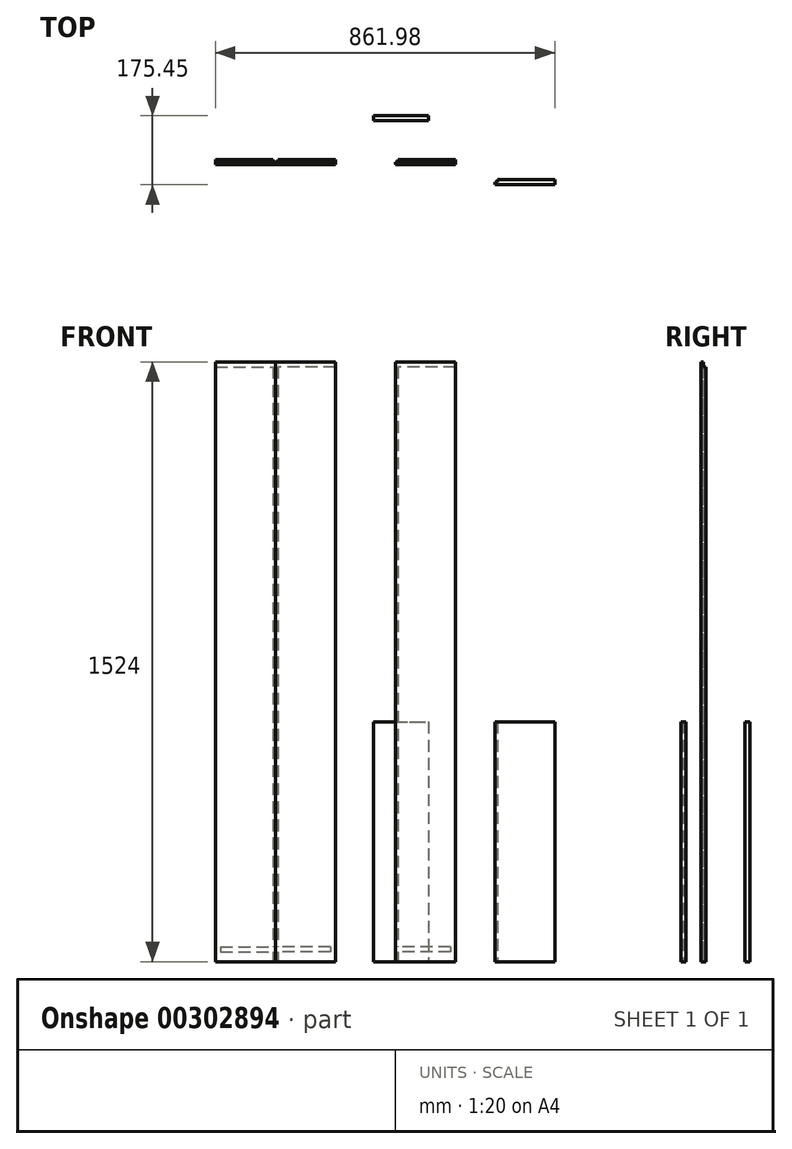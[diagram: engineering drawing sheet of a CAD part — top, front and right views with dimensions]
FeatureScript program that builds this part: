
annotation { "Feature Type Name" : "Feature", "Feature Type Description" : "" }
export const myFeature = defineFeature(function(context is Context, id is Id, definition is map)
    precondition{}
    {
        {
            var Q0;
            Q0=qCreatedBy(makeId("Top.planeOp"),FACE);
            var sketch = newSketch(context, id + "F0", { "sketchPlane" : qUnion([Q0])});
            skLineSegment(sketch, "E0.bottom", {"start": v(0, 0) * mm, "end": v(152.4, 0) * mm});
            skLineSegment(sketch, "E0.top", {"start": v(6.35, 12.7) * mm, "end": v(152.4, 12.7) * mm});
            skLineSegment(sketch, "E0.left", {"start": v(0, 0) * mm, "end": v(0, 6.35) * mm});
            skLineSegment(sketch, "E0.right", {"start": v(152.4, 0) * mm, "end": v(152.4, 12.7) * mm});
            skLineSegment(sketch, "E1.top", {"start": v(0, 6.35) * mm, "end": v(6.35, 6.35) * mm});
            skLineSegment(sketch, "E1.right", {"start": v(6.35, 12.7) * mm, "end": v(6.35, 6.35) * mm});
            skSolve(sketch);
        }
        {
            var Q0;
            Q0 = qSketchRegion(id + "F0", true);
            extrude(context, id + "F1", {"entities" : qUnion([Q0]), "depth" : 1524 * mm});
        }
        {
            var Q0;
            Q0=qCreatedBy(makeId("Top.planeOp"),FACE);
            var sketch = newSketch(context, id + "F2", { "sketchPlane" : qUnion([Q0])});
            skLineSegment(sketch, "E2.bottom", {"start": v(-52.42, -50.86) * mm, "end": v(99.98, -50.86) * mm});
            skLineSegment(sketch, "E2.top", {"start": v(-46.07, -38.16) * mm, "end": v(99.98, -38.16) * mm});
            skLineSegment(sketch, "E2.left", {"start": v(-52.42, -50.86) * mm, "end": v(-52.42, -44.51) * mm});
            skLineSegment(sketch, "E2.right", {"start": v(99.98, -50.86) * mm, "end": v(99.98, -38.16) * mm});
            skLineSegment(sketch, "E3.top", {"start": v(-52.42, -44.51) * mm, "end": v(-46.07, -44.51) * mm});
            skLineSegment(sketch, "E3.right", {"start": v(-46.07, -38.16) * mm, "end": v(-46.07, -44.51) * mm});
            skSolve(sketch);
        }
        {
            var Q0;
            Q0=makeQuery(id+"F2.imprint","IMPRINT",FACE,{"disambiguationData":[TD([[makeQuery(id+"F2.imprint","IMPRINT",EDGE,{"derivedFrom":sQuery(id+"F2.wireOp",EDGE,"E2.bottom")}),1.0]])]});
            extrude(context, id + "F3", {"entities" : qUnion([Q0]), "depth" : 609.6 * mm});
        }
        {
            var Q0;
            Q0=makeQuery(id+"F3.opExtrude","SWEPT_BODY",BODY,{"disambiguationData":[OSD([sQuery(id+"F2.wireOp",EDGE,"E2.bottom"),sQuery(id+"F2.wireOp",EDGE,"E2.top"),sQuery(id+"F2.wireOp",EDGE,"E2.left"),sQuery(id+"F2.wireOp",EDGE,"E2.right"),sQuery(id+"F2.wireOp",EDGE,"E3.top"),sQuery(id+"F2.wireOp",EDGE,"E3.right")])]});
            var Q1;
            Q1=makeQuery(id+"F3.opExtrude","CAP_EDGE",EDGE,{"disambiguationData":[OSD([sQuery(id+"F2.wireOp",EDGE,"E2.bottom")])],"isStart":false});
            transform(context, id + "F4", {"entities" : qUnion([Q0]), "transformType" : TransformType.TRANSLATION_ENTITY, "oppositeDirectionEntity" : false, "transformLine" : qUnion([Q1]), "makeCopy" : false});
        }
        {
            var Q0;
            Q0=makeQuery(id+"F3.opExtrude","SWEPT_BODY",BODY,{"disambiguationData":[OSD([sQuery(id+"F2.wireOp",EDGE,"E2.bottom"),sQuery(id+"F2.wireOp",EDGE,"E2.top"),sQuery(id+"F2.wireOp",EDGE,"E2.left"),sQuery(id+"F2.wireOp",EDGE,"E2.right"),sQuery(id+"F2.wireOp",EDGE,"E3.top"),sQuery(id+"F2.wireOp",EDGE,"E3.right")])]});
            var Q1;
            Q1=makeQuery(id+"F3.opExtrude","CAP_EDGE",EDGE,{"disambiguationData":[OSD([sQuery(id+"F2.wireOp",EDGE,"E2.bottom")])],"isStart":false});
            transform(context, id + "F5", {"entities" : qUnion([Q0]), "transformType" : TransformType.TRANSLATION_ENTITY, "oppositeDirectionEntity" : false, "transformLine" : qUnion([Q1]), "makeCopy" : false});
        }
        {
            var Q0;
            Q0=makeQuery(id+"F1.opExtrude","SWEPT_FACE",FACE,{"disambiguationData":[OSD([sQuery(id+"F0.wireOp",EDGE,"E0.top")])]});
            var sketch = newSketch(context, id + "F6", { "sketchPlane" : qUnion([Q0])});
            skLineSegment(sketch, "E4.bottom", {"start": v(-139.7, 25.4) * mm, "end": v(-6.35, 25.4) * mm});
            skLineSegment(sketch, "E4.top", {"start": v(-139.7, 38.1) * mm, "end": v(-6.35, 38.1) * mm});
            skLineSegment(sketch, "E4.right", {"start": v(-6.35, 25.4) * mm, "end": v(-6.35, 38.1) * mm});
            skLineSegment(sketch, "E5", {"start": v(-139.7, 38.1) * mm, "end": v(-139.7, 25.4) * mm});
            skPoint(sketch, "E6.orphan", {"position": v(-152.4, 25.4) * mm});
            skSolve(sketch);
        }
        {
            var Q0;
            Q0 = qSketchRegion(id + "F6", true);
            extrude(context, id + "F7", {"entities" : qUnion([Q0]), "operationType" : NewBodyOperationType.REMOVE, "oppositeDirection" : true, "depth" : 6.35 * mm});
        }
        {
            var Q0;
            Q0=makeQuery(id+"F1.opExtrude","SWEPT_FACE",FACE,{"disambiguationData":[OSD([sQuery(id+"F0.wireOp",EDGE,"E0.top")])]});
            var sketch = newSketch(context, id + "F8", { "sketchPlane" : qUnion([Q0])});
            skLineSegment(sketch, "E7.bottom", {"start": v(-152.4, 1524) * mm, "end": v(-6.35, 1524) * mm});
            skLineSegment(sketch, "E7.top", {"start": v(-152.4, 1511.3) * mm, "end": v(-6.35, 1511.3) * mm});
            skLineSegment(sketch, "E7.left", {"start": v(-152.4, 1524) * mm, "end": v(-152.4, 1511.3) * mm});
            skLineSegment(sketch, "E7.right", {"start": v(-6.35, 1524) * mm, "end": v(-6.35, 1511.3) * mm});
            skSolve(sketch);
        }
        {
            var Q0;
            Q0 = qSketchRegion(id + "F8", true);
            extrude(context, id + "F9", {"entities" : qUnion([Q0]), "operationType" : NewBodyOperationType.REMOVE, "oppositeDirection" : true, "depth" : 6.35 * mm});
        }
        {
            var Q0;
            Q0=makeQuery(id+"F1.opExtrude","SWEPT_BODY",BODY,{"disambiguationData":[OSD([sQuery(id+"F0.wireOp",EDGE,"E0.bottom"),sQuery(id+"F0.wireOp",EDGE,"E0.top"),sQuery(id+"F0.wireOp",EDGE,"E0.left"),sQuery(id+"F0.wireOp",EDGE,"E0.right"),sQuery(id+"F0.wireOp",EDGE,"E1.top"),sQuery(id+"F0.wireOp",EDGE,"E1.right")])]});
            transform(context, id + "F10", {"entities" : qUnion([Q0]), "transformType" : TransformType.TRANSLATION_3D, "dx" : -304.8 * mm, "dy" : 0 * mm, "dz" : 0 * mm, "makeCopy" : true});
        }
        {
            var Q0;
            Q0=makeQuery(id+"F10.opPattern","COPY",BODY,{"derivedFrom":makeQuery(id+"F1.opExtrude","SWEPT_BODY",BODY,{"disambiguationData":[OSD([sQuery(id+"F0.wireOp",EDGE,"E0.bottom"),sQuery(id+"F0.wireOp",EDGE,"E0.top"),sQuery(id+"F0.wireOp",EDGE,"E0.left"),sQuery(id+"F0.wireOp",EDGE,"E0.right"),sQuery(id+"F0.wireOp",EDGE,"E1.top"),sQuery(id+"F0.wireOp",EDGE,"E1.right")])]}),"instanceName":"1"});
            var Q1;
            Q1=makeQuery(id+"F10.opPattern","COPY",FACE,{"derivedFrom":makeQuery(id+"F1.opExtrude","SWEPT_FACE",FACE,{"disambiguationData":[OSD([sQuery(id+"F0.wireOp",EDGE,"E0.left")])]}),"instanceName":"1"});
            mirror(context, id + "F11", {"entities" : qUnion([Q0]), "mirrorPlane" : qUnion([Q1])});
        }
        {
            var Q0;
            Q0=qCreatedBy(makeId("Top.planeOp"),FACE);
            var sketch = newSketch(context, id + "F12", { "sketchPlane" : qUnion([Q0])});
            skLineSegment(sketch, "E8.bottom", {"start": v(-55.95, 124.59) * mm, "end": v(83.75, 124.59) * mm});
            skLineSegment(sketch, "E8.top", {"start": v(-55.95, 111.89) * mm, "end": v(83.75, 111.89) * mm});
            skLineSegment(sketch, "E8.left", {"start": v(-55.95, 124.59) * mm, "end": v(-55.95, 111.89) * mm});
            skLineSegment(sketch, "E8.right", {"start": v(83.75, 124.59) * mm, "end": v(83.75, 111.89) * mm});
            skSolve(sketch);
        }
        {
            var Q0;
            Q0 = qSketchRegion(id + "F12", true);
            extrude(context, id + "F13", {"entities" : qUnion([Q0]), "depth" : 609.6 * mm});
        }
    });
